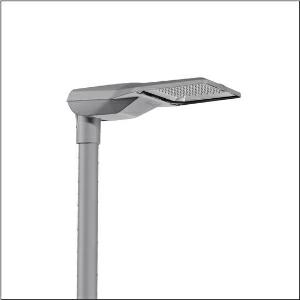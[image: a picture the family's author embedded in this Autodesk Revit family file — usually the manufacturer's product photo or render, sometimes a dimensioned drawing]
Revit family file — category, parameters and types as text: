
# Revit family: streetlight_sl_21_midi___st0_8a_5xe7c23a08lb_df95
name_source: partatom
category: Lighting Fixtures
units: mm (PartAtom-declared; Revit-internal decimal feet)

## family parameters
Cut with Voids When Loaded = No
Host = Face
Light Source = No
Part Type = Normal
Room Calculation Point = No
Round Connector Dimension = Use Diameter
Shared = No

## types (1)
- --- (1 x LED, 11880 lm, 98.3 W, 2200K)
    Apparent Load = 98 VA
    CIE Flux Codes = 38 75 97 100 100
    Color Rendering = 70
    Color Temperature = 2200K
    Default Elevation = 1800 mm
    Description = Streetlight SL 21 midi, mast luminaire, primary light control with lens, of PMMA, primary optical cover: cover, of toughened safety glass, transparent, light distribution: ST0.8a, light emission: direct distribution, primary light characteristic: asymmetric, installation type: post-top, side-entry, LED, 3G 1.5mm², High Power LED, rated luminous flux: 11.880lm, luminous efficacy: 121lm/W, light colour: 722, colour temperature: 2200K, control: overheat protection, constant luminous flux control, time-dependent luminous flux control, flexible luminous flux parameterisation, mains connection: 220..240V, AC, 50/60Hz, connection cable pre-assembled, cable length: 10,5m, wiring characteristics: H07RN-F, start of lifetime: 98W, end of service life: 101W, reduction: 44W, luminaire housing, of diecast aluminium, powder-coated, Siteco® metallic grey (DB 702S), corrosivity category C5 mid according to DIN EN ISO 12944, please order mast flange separately, inclination adjustable: 0°, 5°, 10°, 15°, sealing non-destructively replaceable, multi-level sealing system, length: 644mm, width: 335mm, height: 110mm, mast flange for spigot size: 42mm (side-entry): 5XC10008XM4, 60/48mm (side-entry/post-top): 5XC10108XM2, 76/60mm (side-entry/post-top): 5XC10108XM1, protection rating (complete): IP66, insulation class (complete): insulation class II (safety insulation), certification: CE, ENEC, ENEC+, VDE, impact resistance: IK09, permissible operating ambient temperature for outdoor applications: -40..+50°C, standard-compliant lighting for roads and squares, packaging unit: 1 piece

Light Distribution: ST0.8a
    Height = 111 mm
    Lamp = 1 x LED
    Lamp Light Flux = 11880 lm
    Lamp Power = 98.3 W
    Lamp count = 1
    Length = 644 mm
    Luminous efficacy = 121 lm/W
    Manufacturer = Siteco
    ModVariant = No
    Model = 5XE7C23A08LB
    Number of Poles = 1
    OnlyDefault = Yes
    Power Factor = 1
    Product Name = Streetlight SL 21 midi | ST0.8a
    Product group = mast luminaire | pylon top
    ProductGroupID = 6100
    Protection Class = Protection class II
    Protection Degree = IP 66
    RLX_Detail_Level = 1
    RLX_Emergency_Light_Flux = 0 lm
    RLX_Emergency_Type = 0
    RLX_Emergency_Type_DB = No
    RlxData = <blob elided: 90445 chars, md5=378840df>
    Socket = socket
    Standby Power = 0 W
    System Light Flux = 11880 lm
    System Power = 98 W
    Type Comments = factory setting: luminous flux: 100 % | Output Level: 100 % | 1020 mA
    Type Image = l_1004298.jpg
    URL = http://relux.com
    VarID = @adj_157609
    Voltage = 0 V
    Weight = 0.00 kg
    Width = 336 mm

## geometry (parser evidence)
native form markers: Blend x4, Sweep x11
no freeform markers — native parametric forms only
